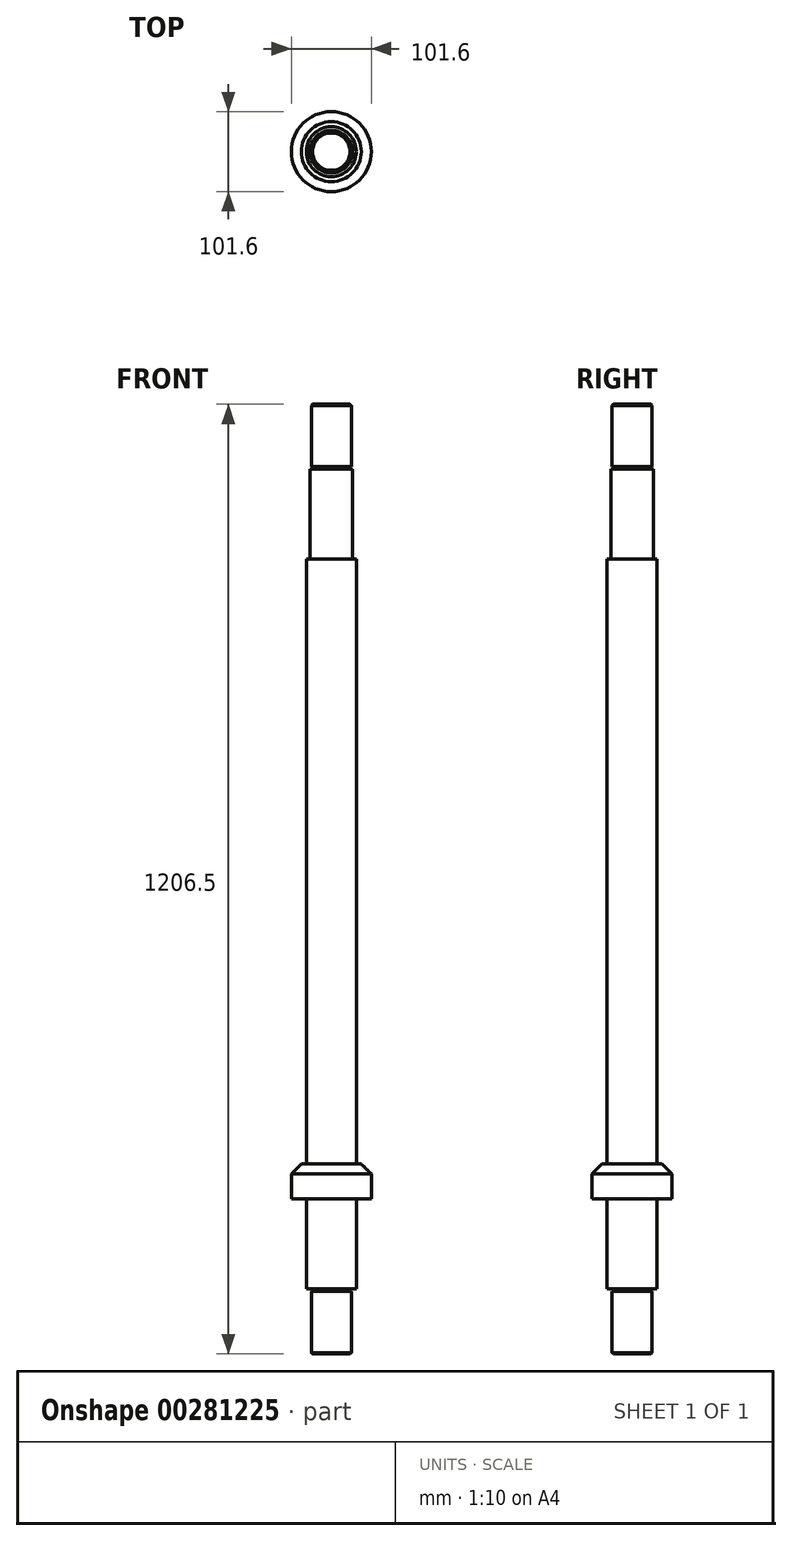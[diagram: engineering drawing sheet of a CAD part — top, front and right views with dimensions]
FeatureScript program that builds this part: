
annotation { "Feature Type Name" : "Feature", "Feature Type Description" : "" }
export const myFeature = defineFeature(function(context is Context, id is Id, definition is map)
    precondition{}
    {
        {
            var Q0;
            Q0=qCreatedBy(makeId("Top.planeOp"),FACE);
            var sketch = newSketch(context, id + "F0", { "sketchPlane" : qUnion([Q0])});
            skCircle(sketch, "E0", {"center": v(0, 0) * mm, "radius": 31.75 * mm});
            skSolve(sketch);
        }
        {
            var Q0;
            Q0 = qSketchRegion(id + "F0", true);
            extrude(context, id + "F1", {"entities" : qUnion([Q0]), "oppositeDirection" : true, "depth" : 114.3 * mm});
        }
        {
            var Q0;
            Q0=makeQuery(id+"F1.opExtrude","CAP_FACE",FACE,{"disambiguationData":[OSD([sQuery(id+"F0.wireOp",EDGE,"E0")])],"isStart":false});
            var sketch = newSketch(context, id + "F2", { "sketchPlane" : qUnion([Q0])});
            skCircle(sketch, "E1", {"center": v(0, 0) * mm, "radius": 23.88 * mm});
            skSolve(sketch);
        }
        {
            var Q0;
            Q0 = qSketchRegion(id + "F2", true);
            extrude(context, id + "F3", {"entities" : qUnion([Q0]), "operationType" : NewBodyOperationType.ADD, "depth" : 3.17 * mm});
        }
        {
            var Q0;
            Q0=makeQuery(id+"F3.opExtrude","CAP_FACE",FACE,{"disambiguationData":[OSD([sQuery(id+"F2.wireOp",EDGE,"E1")])],"isStart":false});
            var sketch = newSketch(context, id + "F4", { "sketchPlane" : qUnion([Q0])});
            skCircle(sketch, "E2", {"center": v(0, 0) * mm, "radius": 25.4 * mm});
            skSolve(sketch);
        }
        {
            var Q0;
            Q0 = qSketchRegion(id + "F4", true);
            extrude(context, id + "F5", {"entities" : qUnion([Q0]), "operationType" : NewBodyOperationType.ADD, "depth" : 79.38 * mm});
        }
        {
            var Q0;
            Q0=makeQuery(id+"F5.opExtrude","CAP_FACE",FACE,{"disambiguationData":[OSD([sQuery(id+"F4.wireOp",EDGE,"E2")])],"isStart":false});
            chamfer(context, id + "F6", {"entities" : qUnion([Q0]), "width" : 1.6 * mm, "tangentPropagation" : true});
        }
        {
            var Q0;
            Q0=makeQuery(id+"F1.opExtrude","CAP_FACE",FACE,{"disambiguationData":[OSD([sQuery(id+"F0.wireOp",EDGE,"E0")])],"isStart":true});
            var sketch = newSketch(context, id + "F7", { "sketchPlane" : qUnion([Q0])});
            skCircle(sketch, "E3", {"center": v(0, 0) * mm, "radius": 50.8 * mm});
            skSolve(sketch);
        }
        {
            var Q0;
            Q0 = qSketchRegion(id + "F7", true);
            extrude(context, id + "F8", {"entities" : qUnion([Q0]), "operationType" : NewBodyOperationType.ADD, "depth" : 44.45 * mm});
        }
        {
            var Q0;
            Q0=makeQuery(id+"F8.opExtrude","CAP_EDGE",EDGE,{"disambiguationData":[OSD([sQuery(id+"F7.wireOp",EDGE,"E3")])],"isStart":false});
            chamfer(context, id + "F9", {"entities" : qUnion([Q0]), "width" : 12.7 * mm, "tangentPropagation" : true});
        }
        {
            var Q0;
            Q0=makeQuery(id+"F8.opExtrude","CAP_FACE",FACE,{"disambiguationData":[OSD([sQuery(id+"F7.wireOp",EDGE,"E3")])],"isStart":false});
            var sketch = newSketch(context, id + "F10", { "sketchPlane" : qUnion([Q0])});
            skCircle(sketch, "E4", {"center": v(0, 0) * mm, "radius": 31.75 * mm});
            skSolve(sketch);
        }
        {
            var Q0;
            Q0 = qSketchRegion(id + "F10", true);
            extrude(context, id + "F11", {"entities" : qUnion([Q0]), "operationType" : NewBodyOperationType.ADD, "depth" : 768.35 * mm});
        }
        {
            var Q0;
            Q0=makeQuery(id+"F11.opExtrude","CAP_FACE",FACE,{"disambiguationData":[OSD([sQuery(id+"F10.wireOp",EDGE,"E4")])],"isStart":false});
            var sketch = newSketch(context, id + "F12", { "sketchPlane" : qUnion([Q0])});
            skCircle(sketch, "E5", {"center": v(0, 0) * mm, "radius": 26.99 * mm});
            skSolve(sketch);
        }
        {
            var Q0;
            Q0 = qSketchRegion(id + "F12", true);
            extrude(context, id + "F13", {"entities" : qUnion([Q0]), "operationType" : NewBodyOperationType.ADD, "depth" : 114.3 * mm});
        }
        {
            var Q0;
            Q0=makeQuery(id+"F13.opExtrude","CAP_FACE",FACE,{"disambiguationData":[OSD([sQuery(id+"F12.wireOp",EDGE,"E5")])],"isStart":false});
            var sketch = newSketch(context, id + "F14", { "sketchPlane" : qUnion([Q0])});
            skCircle(sketch, "E6", {"center": v(0, 0) * mm, "radius": 23.88 * mm});
            skSolve(sketch);
        }
        {
            var Q0;
            Q0 = qSketchRegion(id + "F14", true);
            extrude(context, id + "F15", {"entities" : qUnion([Q0]), "operationType" : NewBodyOperationType.ADD, "depth" : 3.17 * mm});
        }
        {
            var Q0;
            Q0=makeQuery(id+"F15.opExtrude","CAP_FACE",FACE,{"disambiguationData":[OSD([sQuery(id+"F14.wireOp",EDGE,"E6")])],"isStart":false});
            var sketch = newSketch(context, id + "F16", { "sketchPlane" : qUnion([Q0])});
            skCircle(sketch, "E7", {"center": v(0, 0) * mm, "radius": 25.4 * mm});
            skSolve(sketch);
        }
        {
            var Q0;
            Q0 = qSketchRegion(id + "F16", true);
            extrude(context, id + "F17", {"entities" : qUnion([Q0]), "operationType" : NewBodyOperationType.ADD, "depth" : 79.38 * mm});
        }
        {
            var Q0;
            Q0=makeQuery(id+"F17.opExtrude","CAP_FACE",FACE,{"disambiguationData":[OSD([sQuery(id+"F16.wireOp",EDGE,"E7")])],"isStart":false});
            chamfer(context, id + "F18", {"entities" : qUnion([Q0]), "width" : 1.6 * mm, "tangentPropagation" : true});
        }
    });
